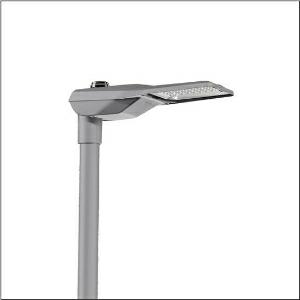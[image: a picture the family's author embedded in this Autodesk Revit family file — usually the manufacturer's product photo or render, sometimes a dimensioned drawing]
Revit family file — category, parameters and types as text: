
# Revit family: streetlight_sl_21_mini___p0_8a_5xe6u67n08hb_4629
name_source: partatom
category: Lighting Fixtures
units: mm (PartAtom-declared; Revit-internal decimal feet)

## family parameters
Cut with Voids When Loaded = No
Host = Face
Light Source = No
Part Type = Normal
Room Calculation Point = No
Round Connector Dimension = Use Diameter
Shared = No

## types (1)
- --- (1 x LED, 8180 lm, 66 W, 2700K)
    Apparent Load = 66 VA
    CIE Flux Codes = 33 69 96 100 100
    Color Rendering = 70
    Color Temperature = 2700K
    Default Elevation = 1800 mm
    Description = Streetlight SL 21 mini, mast luminaire, primary light control with lens, of PMMA, primary optical cover: cover, of toughened safety glass, transparent, light distribution: P0.8a, light emission: direct distribution, primary light characteristic: asymmetric, installation type: side-entry, LED, 3G 1.5mm², High Power LED, rated luminous flux: 8.180lm, luminous efficacy: 124lm/W, light colour: 727, colour temperature: 2700K, control gear: NEMA (7pin), control: flexible luminous flux parameterisation, time-dependent luminous flux control, constant luminous flux control, pre-setting: linear dimming characteristic, overheat protection, mains connection: 230..240V, AC, 50/60Hz, connection cable pre-assembled, cable length: 8,5m, wiring characteristics: H07RN-F, start of lifetime: 66W, end of service life: 69W, reduction: 30W, luminaire housing, of diecast aluminium (EN AC-44300), powder-coated, SITECO metallic grey (DB 702S), corrosivity category C5 high according to DIN EN ISO 12944, multi-level sealing system, sealing non-destructively replaceable, inclination adjustable: 0°, 5°, 10°, 15°, length: 628mm, width: 235mm, height: 110mm, spigot size: 42mm (side-entry), mounting height: 4..8m, protection rating (complete): IP66, insulation class (complete): insulation class I (protective earthing), certification: CE, ENEC, ENEC+, VDE, impact resistance: IK10, permissible operating ambient temperature for outdoor applications: -40..+50°C, standard-compliant lighting for roads and squares, packaging unit: 1 piece

Light Distribution: P0.8a
    Height = 110 mm
    Lamp = 1 x LED
    Lamp Light Flux = 8180 lm
    Lamp Power = 66 W
    Lamp count = 1
    Length = 625 mm
    Luminous efficacy = 124 lm/W
    Manufacturer = Siteco
    ModVariant = No
    Model = 5XE6U67N08HB
    Number of Poles = 1
    OnlyDefault = Yes
    Power Factor = 1
    Product Name = Streetlight SL 21 mini | P0.8a
    Product group = mast luminaire | pylon top
    ProductGroupID = 6100
    Protection Class = Protection class I
    Protection Degree = IP 66
    RLX_Detail_Level = 1
    RLX_Emergency_Light_Flux = 0 lm
    RLX_Emergency_Type = 0
    RLX_Emergency_Type_DB = No
    RlxData = <blob elided: 93645 chars, md5=422a9fb6>
    Socket = socket
    Standby Power = 0 W
    System Light Flux = 8180 lm
    System Power = 66 W
    Type Comments = factory setting: luminous flux: 100 % | dim-lin: 254 | 670 mA
    Type Image = l_1294379.jpg
    URL = http://relux.com
    VarID = @adj_081127
    Voltage = 0 V
    Weight = 0.00 kg
    Width = 234 mm

## geometry (parser evidence)
native form markers: Blend x4, Sweep x10
no freeform markers — native parametric forms only
